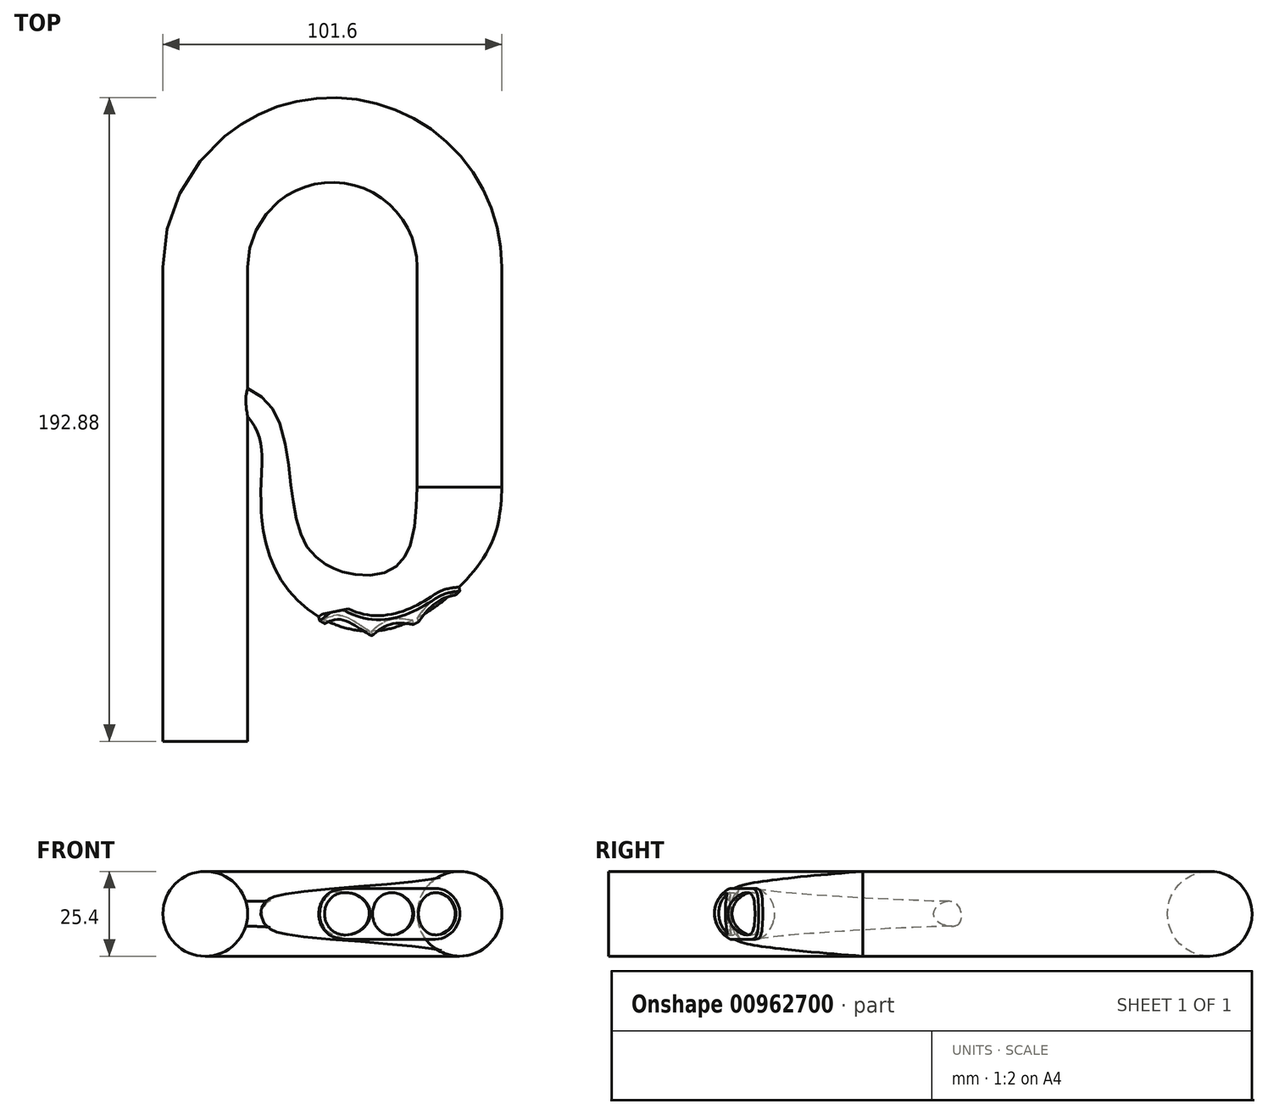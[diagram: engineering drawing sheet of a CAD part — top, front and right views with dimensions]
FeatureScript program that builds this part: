
annotation { "Feature Type Name" : "Feature", "Feature Type Description" : "" }
export const myFeature = defineFeature(function(context is Context, id is Id, definition is map)
    precondition{}
    {
        {
            var Q0;
            Q0=qCreatedBy(makeId("Top.planeOp"),FACE);
            var sketch = newSketch(context, id + "F0", { "sketchPlane" : qUnion([Q0])});
            skLineSegment(sketch, "E0", {"start": v(-40.43, 32.8) * mm, "end": v(-40.43, -33.07) * mm});
            skLineSegment(sketch, "E1", {"start": v(35.77, -33.07) * mm, "end": v(35.77, 32.8) * mm});
            skArc(sketch, "E2", {"start": v(35.77, 32.8) * mm, "mid": v(-2.33, 70.9) * mm, "end": v(-40.43, 32.8) * mm});
            skLineSegment(sketch, "E3", {"start": v(-40.43, -33.07) * mm, "end": v(-40.43, -109.27) * mm});
            skLineSegment(sketch, "E4", {"start": v(35.77, -33.07) * mm, "end": v(35.77, -83.92) * mm});
            skLineSegment(sketch, "E5", {"start": v(-40.43, -33.07) * mm, "end": v(-40.43, 0) * mm});
            skFitSpline(sketch, "E6", {"points": [v(35.77, -33.07) * mm, v(27.33, -59.85) * mm, v(1.28, -66.87) * mm, v(-18.72, -44.71) * mm, v(-21.18, -14.35) * mm, v(-40.43, 0) * mm], "startDerivative": vector(-41.13, -142.06) * mm, "endDerivative": vector(-37.04, 81.09) * mm});
            skLineSegment(sketch, "E7", {"start": v(-40.43, 0) * mm, "end": v(-40.43, 32.8) * mm});
            skPoint(sketch, "E8", {"position": v(15.64, -74.81) * mm});
            skPoint(sketch, "E9", {"position": v(14.08, -67.22) * mm});
            skLineSegment(sketch, "E10", {"start": v(14.08, -67.22) * mm, "end": v(15.64, -74.81) * mm});
            skSolve(sketch);
        }
        {
            var Q0;
            Q0=qCreatedBy(makeId("Front.planeOp"),FACE);
            var sketch = newSketch(context, id + "F1", { "sketchPlane" : qUnion([Q0])});
            skPoint(sketch, "E11.0", {"position": v(-40.43, 0) * mm});
            skCircle(sketch, "E12", {"center": v(-40.43, 0) * mm, "radius": 12.7 * mm});
            skCircle(sketch, "E13", {"center": v(-40.43, 0) * mm, "radius": 3.81 * mm});
            skSolve(sketch);
        }
        {
            var Q0;
            Q0=makeQuery(id+"F1.imprint","IMPRINT",FACE,{"disambiguationData":[TD([[makeQuery(id+"F1.imprint","IMPRINT",EDGE,{"derivedFrom":sQuery(id+"F1.wireOp",EDGE,"E12")}),1.0]])]});
            var Q1;
            Q1=makeQuery(id+"F1.imprint","IMPRINT",FACE,{"disambiguationData":[TD([[makeQuery(id+"F1.imprint","IMPRINT",EDGE,{"derivedFrom":sQuery(id+"F1.wireOp",EDGE,"E13")}),1.0]])]});
            var Q2;
            Q2=sQuery(id+"F0.wireOp",EDGE,"E7");
            var Q3;
            Q3=sQuery(id+"F0.wireOp",EDGE,"E1");
            var Q4;
            Q4=sQuery(id+"F0.wireOp",EDGE,"E2");
            sweep(context, id + "F2", {"profiles" : qUnion([Q0, Q1]), "path" : qUnion([Q2, Q3, Q4])});
        }
        {
            var Q0;
            Q0 = qSketchRegion(id + "F1", true);
            var Q1;
            Q1=makeQuery(id+"F1.imprint","IMPRINT",FACE,{"disambiguationData":[TD([[makeQuery(id+"F1.imprint","IMPRINT",EDGE,{"derivedFrom":sQuery(id+"F1.wireOp",EDGE,"E13")}),1.0]])]});
            var Q2;
            Q2=sQuery(id+"F0.wireOp",EDGE,"E5");
            var Q3;
            Q3=sQuery(id+"F0.wireOp",EDGE,"E3");
            sweep(context, id + "F3", {"operationType" : NewBodyOperationType.ADD, "profiles" : qUnion([Q0, Q1]), "path" : qUnion([Q2, Q3])});
        }
        {
            var Q0;
            Q0=qCreatedBy(makeId("Front.planeOp"),FACE);
            var sketch = newSketch(context, id + "F4", { "sketchPlane" : qUnion([Q0])});
            skCircle(sketch, "E14.0", {"center": v(-40.43, 0) * mm, "radius": 12.7 * mm});
            skSolve(sketch);
        }
        {
            var Q0;
            Q0=makeQuery(id+"F2.opSweep","CAP_FACE",FACE,{"disambiguationData":[OSD([sQuery(id+"F0.wireOp",VERTEX,"E1.start"),sQuery(id+"F1.wireOp",EDGE,"E12")])],"isStart":false});
            var sketch = newSketch(context, id + "F5", { "sketchPlane" : qUnion([Q0])});
            skCircle(sketch, "E15.0.0", {"center": v(35.77, 0) * mm, "radius": 12.7 * mm});
            skPoint(sketch, "E16", {"position": v(48.47, 0) * mm});
            skPoint(sketch, "E17", {"position": v(23.07, 0) * mm});
            skPoint(sketch, "E18", {"position": v(35.77, 12.7) * mm});
            skPoint(sketch, "E19", {"position": v(35.77, -12.7) * mm});
            skSolve(sketch);
        }
        {
            var Q0;
            Q0=sQuery(id+"F0.wireOp",EDGE,"E6");
            var Q1;
            Q1=makeQuery(id+"F1.imprint","IMPRINT",FACE,{"disambiguationData":[TD([[makeQuery(id+"F1.imprint","IMPRINT",EDGE,{"derivedFrom":sQuery(id+"F1.wireOp",EDGE,"E13")}),1.0]])]});
            var Q2;
            Q2=makeQuery(id+"F5.imprint","IMPRINT",FACE,{"disambiguationData":[TD([[makeQuery(id+"F5.imprint","IMPRINT",EDGE,{"derivedFrom":sQuery(id+"F5.wireOp",EDGE,"E15.0.0")}),1.0]])]});
            var Q3;
            Q3=sQuery(id+"F0.wireOp",EDGE,"E6");
            loft(context, id + "F6", {"operationType" : NewBodyOperationType.ADD, "addSections" : true, "spine" : qUnion([Q0]), "sectionCount" : 5, "sheetProfilesArray" : [{ "sheetProfileEntities" : qUnion([Q1]) }, { "sheetProfileEntities" : qUnion([Q2]) }], "guidesArray" : [{ "guideEntities" : qUnion([Q3]), "guideDerivativeType" : LoftGuideDerivativeType.DEFAULT, "guideDerivativeMagnitude" : 1 }]});
        }
        {
            var Q0;
            Q0=sQuery(id+"F0.wireOp",EDGE,"E10");
            var Q1;
            Q1=sQuery(id+"F0.wireOp",VERTEX,"E9");
            cPlane(context, id + "F7", {"entities" : qUnion([Q0, Q1]), "cplaneType" : CPlaneType.LINE_POINT, "offset" : 25.4 * mm, "width" : 152.4 * mm, "height" : 152.4 * mm});
        }
        {
            var Q0;
            Q0=qCreatedBy(id+"F7.planeOp",FACE);
            var sketch = newSketch(context, id + "F8", { "sketchPlane" : qUnion([Q0])});
            skPoint(sketch, "E20.0", {"position": v(0.27, 0) * mm});
            skCircle(sketch, "E21", {"center": v(0.27, 0) * mm, "radius": 6.35 * mm});
            skCircle(sketch, "E22", {"center": v(14.54, 0) * mm, "radius": 6.35 * mm});
            skCircle(sketch, "E23", {"center": v(-13.1, 0) * mm, "radius": 6.35 * mm});
            skLineSegment(sketch, "E24", {"start": v(-13.1, 7.62) * mm, "end": v(14.59, 7.62) * mm});
            skLineSegment(sketch, "E25", {"start": v(-13.1, -7.62) * mm, "end": v(14.59, -7.62) * mm});
            skArc(sketch, "E26", {"start": v(-13.1, 7.62) * mm, "mid": v(-20.72, 0) * mm, "end": v(-13.1, -7.62) * mm});
            skArc(sketch, "E27", {"start": v(14.59, -7.62) * mm, "mid": v(22.2, 0) * mm, "end": v(14.59, 7.62) * mm});
            skSolve(sketch);
        }
        {
            var Q0;
            Q0 = qSketchRegion(id + "F8", true);
            var Q1;
            Q1=makeQuery(id+"F6.opLoft","SWEPT_FACE",FACE,{"disambiguationData":[OSD([sQuery(id+"F1.wireOp",EDGE,"E13"),sQuery(id+"F5.wireOp",EDGE,"E15.0.0")])]});
            extrude(context, id + "F9", {"entities" : qUnion([Q0]), "operationType" : NewBodyOperationType.ADD, "endBound" : BoundingType.UP_TO_SURFACE, "depth" : 25.4 * mm, "endBoundEntityFace" : qUnion([Q1]), "hasOffset" : true, "offsetDistance" : -1.27 * mm});
        }
    });
